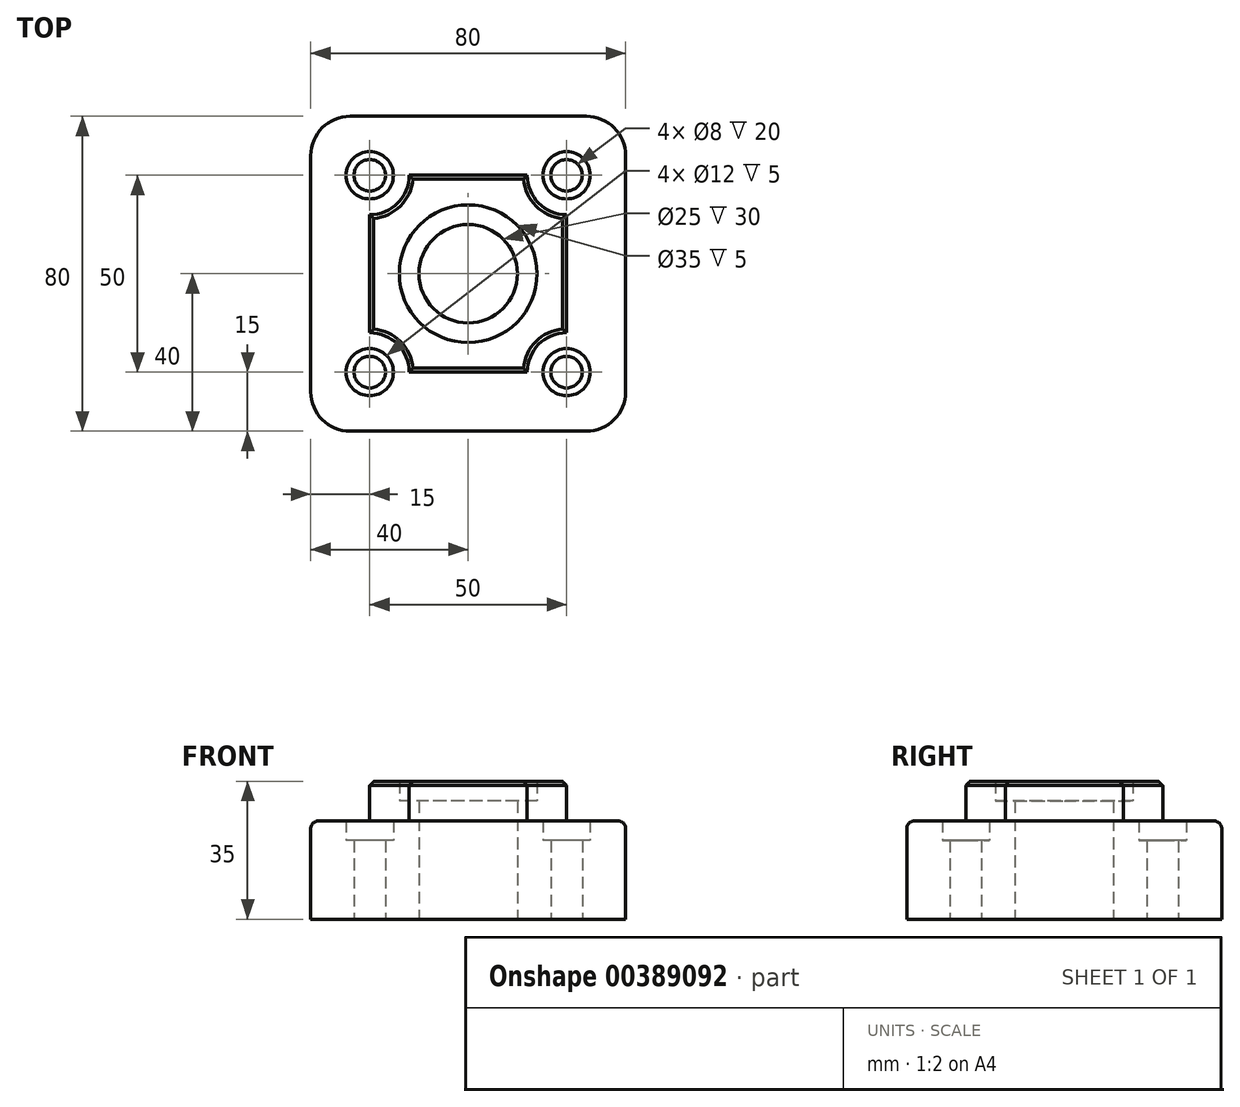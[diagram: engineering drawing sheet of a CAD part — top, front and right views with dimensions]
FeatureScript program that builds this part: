
annotation { "Feature Type Name" : "Feature", "Feature Type Description" : "" }
export const myFeature = defineFeature(function(context is Context, id is Id, definition is map)
    precondition{}
    {
        {
            var Q0;
            Q0=qCreatedBy(makeId("Top.planeOp"),FACE);
            cPlane(context, id + "F0", {"entities" : qUnion([Q0]), "cplaneType" : CPlaneType.OFFSET, "offset" : 25 * mm, "width" : 150 * mm, "height" : 150 * mm});
        }
        {
            var Q0;
            Q0=qCreatedBy(id+"F0.planeOp",FACE);
            cPlane(context, id + "F1", {"entities" : qUnion([Q0]), "cplaneType" : CPlaneType.OFFSET, "offset" : 5 * mm, "width" : 150 * mm, "height" : 150 * mm});
        }
        {
            var Q0;
            Q0=qCreatedBy(makeId("Top.planeOp"),FACE);
            cPlane(context, id + "F2", {"entities" : qUnion([Q0]), "cplaneType" : CPlaneType.OFFSET, "offset" : 20 * mm, "width" : 150 * mm, "height" : 150 * mm});
        }
        {
            var Q0;
            Q0=qCreatedBy(makeId("Top.planeOp"),FACE);
            var sketch = newSketch(context, id + "F3", { "sketchPlane" : qUnion([Q0])});
            skCircle(sketch, "E0", {"center": v(0, 0) * mm, "radius": 12.5 * mm});
            skCircle(sketch, "E1", {"center": v(-25, 25) * mm, "radius": 4 * mm});
            skCircle(sketch, "E2.1.1", {"center": v(25, 25) * mm, "radius": 4 * mm});
            skCircle(sketch, "E2.2.1", {"center": v(25, -25) * mm, "radius": 4 * mm});
            skCircle(sketch, "E2.3.1", {"center": v(-25, -25) * mm, "radius": 4 * mm});
            skLineSegment(sketch, "E2.anchor1", {"start": v(0, 0) * mm, "end": v(-25, 25) * mm, "construction": true});
            skLineSegment(sketch, "E2.anchor2", {"start": v(0, 0) * mm, "end": v(-25, -25) * mm, "construction": true});
            skLineSegment(sketch, "E3.bottom", {"start": v(-30, 40) * mm, "end": v(30, 40) * mm});
            skLineSegment(sketch, "E3.top", {"start": v(-30, -40) * mm, "end": v(30, -40) * mm});
            skLineSegment(sketch, "E3.left", {"start": v(-40, 30) * mm, "end": v(-40, -30) * mm});
            skLineSegment(sketch, "E3.right", {"start": v(40, 30) * mm, "end": v(40, -30) * mm});
            skPoint(sketch, "E4.visualSharp", {"position": v(-40, 40) * mm});
            skArc(sketch, "E4.filletArc", {"start": v(-30, 40) * mm, "mid": v(-37.07, 37.07) * mm, "end": v(-40, 30) * mm});
            skPoint(sketch, "E5.visualSharp", {"position": v(40, 40) * mm});
            skArc(sketch, "E5.filletArc", {"start": v(40, 30) * mm, "mid": v(37.07, 37.07) * mm, "end": v(30, 40) * mm});
            skPoint(sketch, "E6.visualSharp", {"position": v(40, -40) * mm});
            skArc(sketch, "E6.filletArc", {"start": v(30, -40) * mm, "mid": v(37.07, -37.07) * mm, "end": v(40, -30) * mm});
            skPoint(sketch, "E7.visualSharp", {"position": v(-40, -40) * mm});
            skArc(sketch, "E7.filletArc", {"start": v(-40, -30) * mm, "mid": v(-37.07, -37.07) * mm, "end": v(-30, -40) * mm});
            skSolve(sketch);
        }
        {
            var Q0;
            Q0=qCreatedBy(id+"F0.planeOp",FACE);
            var sketch = newSketch(context, id + "F4", { "sketchPlane" : qUnion([Q0])});
            skLineSegment(sketch, "E8.bottom", {"start": v(-15, 25) * mm, "end": v(15, 25) * mm});
            skLineSegment(sketch, "E8.top", {"start": v(-15, -25) * mm, "end": v(15, -25) * mm});
            skLineSegment(sketch, "E8.left", {"start": v(-25, 15) * mm, "end": v(-25, -15) * mm});
            skLineSegment(sketch, "E8.right", {"start": v(25, 15) * mm, "end": v(25, -15) * mm});
            skArc(sketch, "E9", {"start": v(-25, 15) * mm, "mid": v(-17.93, 17.93) * mm, "end": v(-15, 25) * mm});
            skArc(sketch, "E10", {"start": v(15, 25) * mm, "mid": v(17.93, 17.93) * mm, "end": v(25, 15) * mm});
            skArc(sketch, "E11", {"start": v(25, -15) * mm, "mid": v(17.93, -17.93) * mm, "end": v(15, -25) * mm});
            skArc(sketch, "E12", {"start": v(-15, -25) * mm, "mid": v(-17.93, -17.93) * mm, "end": v(-25, -15) * mm});
            skPoint(sketch, "E13.center", {"position": v(0, 0) * mm});
            skCircle(sketch, "E14", {"center": v(0, 0) * mm, "radius": 12.5 * mm});
            skSolve(sketch);
        }
        {
            var Q0;
            Q0=qCreatedBy(id+"F1.planeOp",FACE);
            var sketch = newSketch(context, id + "F5", { "sketchPlane" : qUnion([Q0])});
            skCircle(sketch, "E15", {"center": v(0, 0) * mm, "radius": 17.5 * mm});
            skSolve(sketch);
        }
        {
            var Q0;
            Q0=qCreatedBy(id+"F2.planeOp",FACE);
            var sketch = newSketch(context, id + "F6", { "sketchPlane" : qUnion([Q0])});
            skCircle(sketch, "E16", {"center": v(-25, 25) * mm, "radius": 6 * mm});
            skCircle(sketch, "E17.1.0", {"center": v(25, 25) * mm, "radius": 6 * mm});
            skCircle(sketch, "E17.2.0", {"center": v(25, -25) * mm, "radius": 6 * mm});
            skCircle(sketch, "E17.3.0", {"center": v(-25, -25) * mm, "radius": 6 * mm});
            skSolve(sketch);
        }
        {
            var Q0;
            Q0 = qSketchRegion(id + "F3", true);
            extrude(context, id + "F7", {"entities" : qUnion([Q0]), "depth" : 25 * mm});
        }
        {
            var Q0;
            Q0 = qSketchRegion(id + "F4", true);
            extrude(context, id + "F8", {"entities" : qUnion([Q0]), "operationType" : NewBodyOperationType.ADD, "depth" : 10 * mm});
        }
        {
            var Q0;
            Q0 = qSketchRegion(id + "F5", true);
            extrude(context, id + "F9", {"entities" : qUnion([Q0]), "operationType" : NewBodyOperationType.REMOVE, "depth" : 5 * mm});
        }
        {
            var Q0;
            Q0 = qSketchRegion(id + "F6", true);
            extrude(context, id + "F10", {"entities" : qUnion([Q0]), "operationType" : NewBodyOperationType.REMOVE, "depth" : 5 * mm});
        }
        {
            var Q0;
            Q0=makeQuery(id+"F8.opExtrude","CAP_EDGE",EDGE,{"disambiguationData":[OSD([sQuery(id+"F4.wireOp",EDGE,"E9")])],"isStart":false});
            var Q1;
            Q1=makeQuery(id+"F8.opExtrude","CAP_EDGE",EDGE,{"disambiguationData":[OSD([sQuery(id+"F4.wireOp",EDGE,"E8.left")])],"isStart":false});
            var Q2;
            Q2=makeQuery(id+"F8.opExtrude","CAP_EDGE",EDGE,{"disambiguationData":[OSD([sQuery(id+"F4.wireOp",EDGE,"E12")])],"isStart":false});
            var Q3;
            Q3=makeQuery(id+"F8.opExtrude","CAP_EDGE",EDGE,{"disambiguationData":[OSD([sQuery(id+"F4.wireOp",EDGE,"E8.top")])],"isStart":false});
            var Q4;
            Q4=makeQuery(id+"F8.opExtrude","CAP_EDGE",EDGE,{"disambiguationData":[OSD([sQuery(id+"F4.wireOp",EDGE,"E11")])],"isStart":false});
            var Q5;
            Q5=makeQuery(id+"F8.opExtrude","CAP_EDGE",EDGE,{"disambiguationData":[OSD([sQuery(id+"F4.wireOp",EDGE,"E8.right")])],"isStart":false});
            var Q6;
            Q6=makeQuery(id+"F8.opExtrude","CAP_EDGE",EDGE,{"disambiguationData":[OSD([sQuery(id+"F4.wireOp",EDGE,"E10")])],"isStart":false});
            var Q7;
            Q7=makeQuery(id+"F8.opExtrude","CAP_EDGE",EDGE,{"disambiguationData":[OSD([sQuery(id+"F4.wireOp",EDGE,"E8.bottom")])],"isStart":false});
            chamfer(context, id + "F11", {"entities" : qUnion([Q0, Q1, Q2, Q3, Q4, Q5, Q6, Q7]), "width" : 1 * mm, "tangentPropagation" : true});
        }
        {
            var Q0;
            Q0=makeQuery(id+"F7.opExtrude","CAP_EDGE",EDGE,{"disambiguationData":[OSD([sQuery(id+"F3.wireOp",EDGE,"E7.filletArc")])],"isStart":false});
            var Q1;
            Q1=makeQuery(id+"F7.opExtrude","CAP_EDGE",EDGE,{"disambiguationData":[OSD([sQuery(id+"F3.wireOp",EDGE,"E3.left")])],"isStart":false});
            fillet(context, id + "F12", {"entities" : qUnion([Q0, Q1]), "radius" : 2 * mm, "tangentPropagation" : true, "allowEdgeOverflow" : false});
        }
    });
